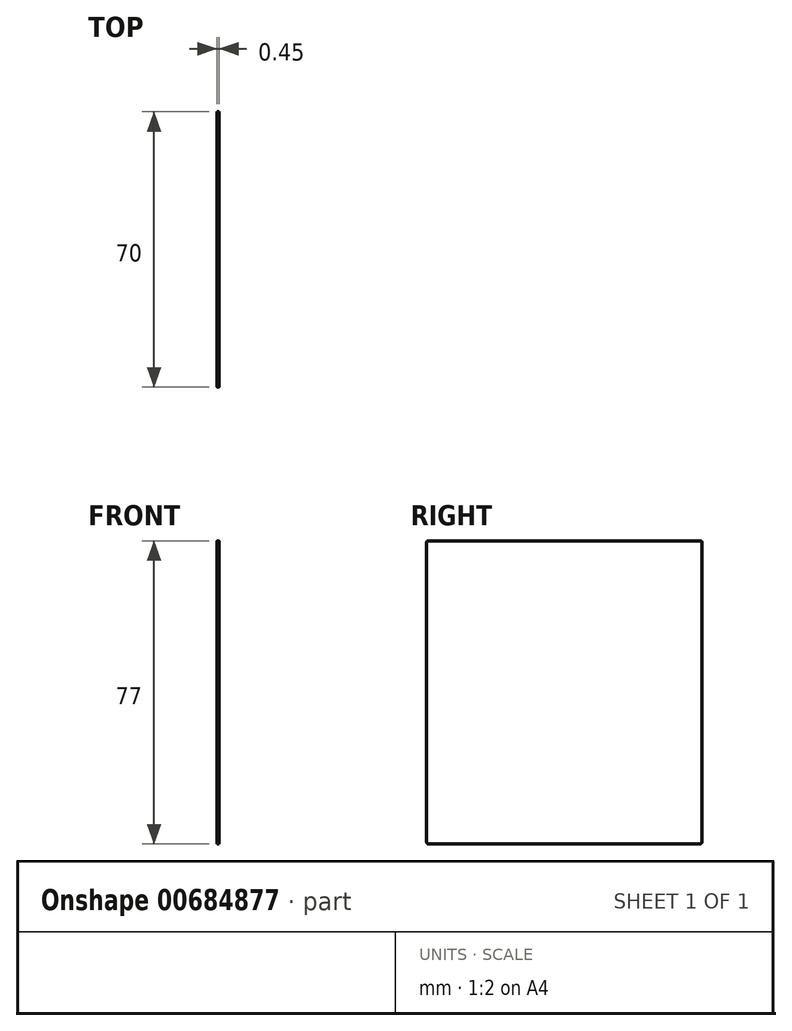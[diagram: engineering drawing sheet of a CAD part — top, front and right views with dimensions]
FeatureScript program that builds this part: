
annotation { "Feature Type Name" : "Feature", "Feature Type Description" : "" }
export const myFeature = defineFeature(function(context is Context, id is Id, definition is map)
    precondition{}
    {
        {
            var Q0;
            Q0=qCreatedBy(makeId("Right.planeOp"),FACE);
            var sketch = newSketch(context, id + "F0", { "sketchPlane" : qUnion([Q0])});
            skLineSegment(sketch, "E0.bottom", {"start": v(0, 0) * mm, "end": v(70, 0) * mm});
            skLineSegment(sketch, "E0.top", {"start": v(0, -77) * mm, "end": v(70, -77) * mm});
            skLineSegment(sketch, "E0.left", {"start": v(0, 0) * mm, "end": v(0, -77) * mm});
            skLineSegment(sketch, "E0.right", {"start": v(70, 0) * mm, "end": v(70, -77) * mm});
            skSolve(sketch);
        }
        {
            var Q0;
            Q0=makeQuery(id+"F0.imprint","IMPRINT",FACE,{"disambiguationData":[TD([[makeQuery(id+"F0.imprint","IMPRINT",EDGE,{"derivedFrom":sQuery(id+"F0.wireOp",EDGE,"E0.bottom")}),-1.0]])]});
            extrude(context, id + "F1", {"entities" : qUnion([Q0]), "depth" : .45 * mm, "offsetDistance" : 25 * mm});
        }
        {
            var Q0;
            Q0=makeQuery(id+"F1.opExtrude","SWEPT_EDGE",EDGE,{"disambiguationData":[OSD([sQuery(id+"F0.wireOp",EDGE,"E0.bottom"),sQuery(id+"F0.wireOp",EDGE,"E0.left")])]});
            var Q1;
            Q1=makeQuery(id+"F1.opExtrude","SWEPT_EDGE",EDGE,{"disambiguationData":[OSD([sQuery(id+"F0.wireOp",EDGE,"E0.bottom"),sQuery(id+"F0.wireOp",EDGE,"E0.right")])]});
            var Q2;
            Q2=makeQuery(id+"F1.opExtrude","SWEPT_EDGE",EDGE,{"disambiguationData":[OSD([sQuery(id+"F0.wireOp",EDGE,"E0.top"),sQuery(id+"F0.wireOp",EDGE,"E0.left")])]});
            var Q3;
            Q3=makeQuery(id+"F1.opExtrude","SWEPT_EDGE",EDGE,{"disambiguationData":[OSD([sQuery(id+"F0.wireOp",EDGE,"E0.top"),sQuery(id+"F0.wireOp",EDGE,"E0.right")])]});
            fillet(context, id + "F2", {"entities" : qUnion([Q0, Q1, Q2, Q3]), "radius" : 0.5 * mm, "tangentPropagation" : true, "allowEdgeOverflow" : false});
        }
    });
